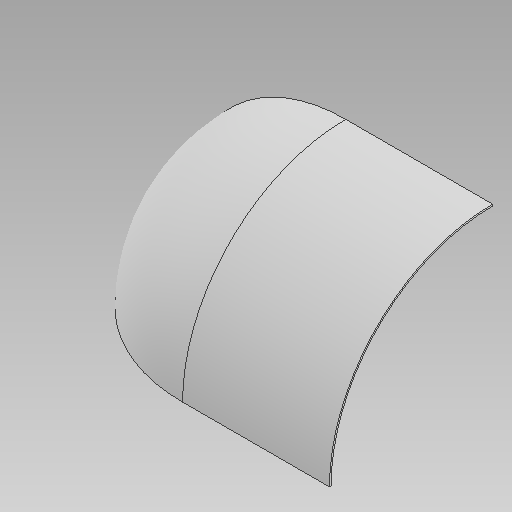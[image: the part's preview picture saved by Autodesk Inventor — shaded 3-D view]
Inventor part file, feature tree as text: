
AUTODESK INVENTOR PART (.ipt)
format: ipt  version: 2021 (Build 250183000, 183)  size: 139,776 bytes
history: native  units: mm
features: sketch x2, revolve x1, extrude x1, other x1
ambient origin geometry x8: Origin, YZ Plane, XZ Plane, XY Plane, X Axis, Y Axis, Z Axis, Center Point
bodies: Body1 (feature_tree)
feature tree (5):
  revolve  "Revolution1"  [1 undecoded]
  extrude  "Extrusion2"  TaperAngle=0.0deg  [1 undecoded]
  other  "tangent1"
  sketch  "Sketch1"  dims[d0=10.0mm d1=1000.0mm]
  sketch  "Sketch2"  dims[d2=0.0mm d3=0.0mm d6=90.0deg d9=900.0mm d10=0.0mm]
note: 2 required parameter values undecoded (feature->parameter linkage not recoverable at this tier; creation-order binding heuristic only, values carry confidence <= 0.55)